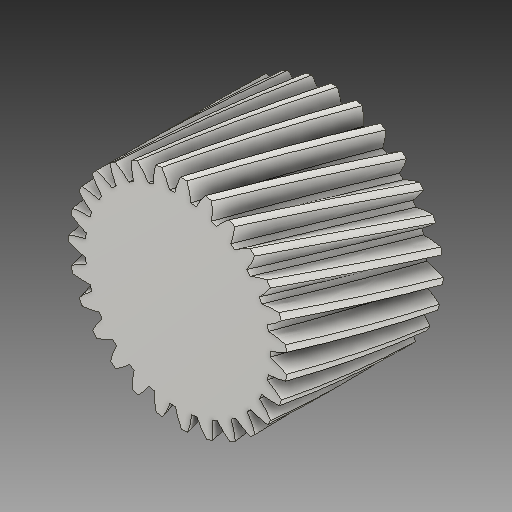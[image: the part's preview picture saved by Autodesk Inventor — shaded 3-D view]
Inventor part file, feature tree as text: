
AUTODESK INVENTOR PART (.ipt)
format: ipt  version: 2020 (Build 240168000, 168)  size: 562,688 bytes
history: native  units: mm (DEFAULTED — no unit token found)
features: plane x3, other x3, sketch x2, extrude x1
ambient origin geometry x8: Origin, YZ Plane, XZ Plane, XY Plane, X Axis, Y Axis, Z Axis, Center Point
bodies: Solid1 (feature_tree)
feature tree (9):
  extrude  "Extrusion1"  Depth=15.0mm TaperAngle=0.0deg
  plane  "Work Plane2"
  plane  "Work Plane8"
  plane  "Work Plane9"
  other  "Spur Gear"
  sketch  "Sketch1"  dims[d0=20.911014mm d1=15.0mm d2=0.0mm]
  sketch  "Sketch2"  dims[d3=19.557549mm d4=10.0mm d5=0.0mm d16=59.397mm d17=0.0mm d34=1.163553mm d39=0.0mm d41=0.0mm d43=59.397mm d46=59.397mm d47=0.0mm d48=0.0mm]
  other  "Srf1"
  other  "Pitch Diameter"
